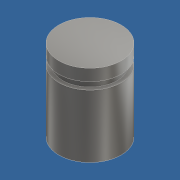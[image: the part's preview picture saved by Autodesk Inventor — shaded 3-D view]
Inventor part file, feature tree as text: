
AUTODESK INVENTOR PART (.ipt)
format: ipt  version: 2018 (Build 220112000, 112)  size: 139,776 bytes
history: native  units: mm
features: other x3, sketch x2, extrude x1, revolve x1, reference x1
ambient origin geometry x8: Origin, YZ Plane, XZ Plane, XY Plane, X Axis, Y Axis, Z Axis, Center Point
bodies: Solid1 (feature_tree)
feature tree (8):
  extrude  "Extrusion1"  Depth=10.5mm TaperAngle=0.0deg
  revolve  "Revolution1"  [1 undecoded]
  sketch  "Sketch1"  dims[d0=8.0mm d1=10.5mm d2=0.0mm]
  sketch  "Sketch2"  dims[d3=0.5mm d4=1.0mm d5=0.94mm d6=1.5mm d7=90.0deg]
  reference  "Reference1"
  other  "<userpath>\OneDrive\Objet3D\EPFLEplucheCarrote\Assembly1.iam"
  other  "Assembly1.iam"
  other  "FeetV3:2"
note: 1 required parameter value undecoded (feature->parameter linkage not recoverable at this tier; creation-order binding heuristic only, values carry confidence <= 0.55)
